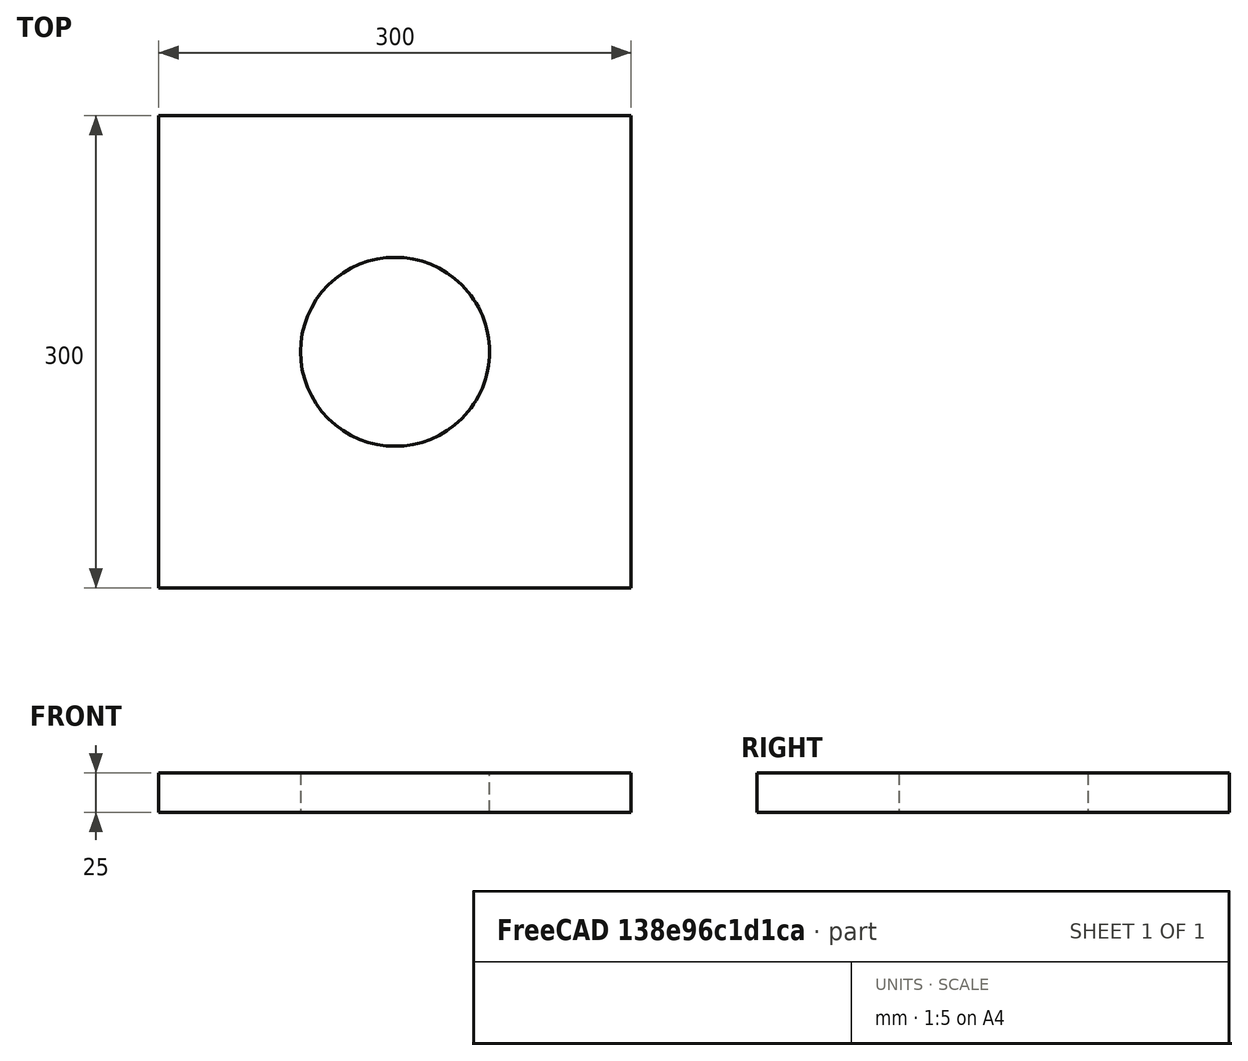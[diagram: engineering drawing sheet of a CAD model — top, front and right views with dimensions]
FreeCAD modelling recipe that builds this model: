
FCSTD DOCUMENT  (FreeCAD 0.21R33694 (Git))
Label: Lug_Pressure_Example
License: All rights reserved
LicenseURL: http://en.wikipedia.org/wiki/All_rights_reserved
objects: Part::FeaturePython×5, Sketcher::SketchObject×2, Part::Extrusion×2, Fem::FemMeshObjectPython×2, Fem::FemSolverObjectPython×1, Fem::ConstraintFixed×1, Part::MultiFuse×1, Fem::ConstraintPressure×1, App::MaterialObjectPython×1, Fem::FemResultObjectPython×1, Fem::FemAnalysis×1
note: 10 computed .brp shape members not serialized (recipe doc carries the construction recipe); baked Part::Feature solids carry a one-line shape summary decoded from their .brp

FEATURE [Sketcher::SketchObject] Sketch
  FullyConstrained = true
  Placement = pos=(150,0,0) rot=(0,0,1;0rad)
  sketch-geometry (5):
    g0: LineSegment StartX=0 StartY=0 StartZ=0 EndX=300 EndY=0 EndZ=0
    g1: LineSegment StartX=300 StartY=0 StartZ=0 EndX=300 EndY=300 EndZ=0
    g2: LineSegment StartX=300 StartY=300 StartZ=0 EndX=0 EndY=300 EndZ=0
    g3: LineSegment StartX=0 StartY=300 StartZ=0 EndX=0 EndY=0 EndZ=0
    g4: Circle CenterX=150 CenterY=150 CenterZ=0 NormalX=0 NormalY=0 NormalZ=1 AngleXU=0 Radius=60
  constraints (14):
    c: Coincident(g0,g1)
    c: Coincident(g1,g2)
    c: Coincident(g2,g3)
    c: Coincident(g3,g0)
    c: Horizontal(g0)
    c: Horizontal(g2)
    c: Vertical(g1)
    c: Vertical(g3)
    c: Coincident(g0,g-1)
    c: DistanceY(g1,g1) = 300
    c: DistanceX(g0,g0) = 300
    c: DistanceX(g0,g4) = 150
    c: DistanceY(g0,g4) = 150
    c: Radius(g4) = 60
FEATURE [Part::Extrusion] Extrude
  Base = -> Sketch
  Dir = (0,0,1)
  DirMode = 2
  FaceMakerClass = Part::FaceMakerBullseye
  LengthFwd = 25
  LengthRev = 0
  Solid = true
  Symmetric = false
FEATURE [Fem::FemSolverObjectPython] SolverCcxTools  # FEM object (typed FeaturePython)
  AnalysisType = 0
  BeamShellResultOutput3D = false
  BucklingFactors = 1
  EigenmodeHighLimit = 1000000
  EigenmodeLowLimit = 0
  EigenmodesCount = 10
  GeometricalNonlinearity = 0
  IterationsControlParameterCutb = 0.25,0.5,0.75,0.85,,,1.5,
  IterationsControlParameterIter = 4,8,9,200,10,400,,200,,
  IterationsControlParameterTimeUse = false
  IterationsThermoMechMaximum = 200
  IterationsUserDefinedIncrementations = false
  IterationsUserDefinedTimeStepLength = false
  MaterialNonlinearity = 0
  MatrixSolverType = 0
  SplitInputWriter = false
  ThermoMechSteadyState = true
  TimeEnd = 1
  TimeInitialStep = 1
FEATURE [Fem::ConstraintFixed] ConstraintFixed001
  NormalDirection = (0,-1,0)
  Normals = (16) [(0,-1,0),(0,-1,0),(0,-1,0),(0,-1,0),(0,-1,0),(0,-1,0),(0,-1,0),(0,-1,0),(0,-1,0),(0,-1,0),(0,-1,0),(0,-1,0),(0,-1,0),(0,-1,0),(0,-1,0),(0,-1,0)]
  Points = (16) [(150,0,25),(250,0,25),(350,0,25),(450,0,25),(150,0,16.6667),(250,0,16.6667),(350,0,16.6667),(450,0,16.6667),(150,0,8.33333),(250,0,8.33333),+6 more]
  References = -> [Extrude]
  Scale = 13
FEATURE [Sketcher::SketchObject] Sketch001
  FullyConstrained = true
  sketch-geometry (2):
    g0: LineSegment StartX=150 StartY=300 StartZ=0 EndX=450 EndY=0 EndZ=0
    g1: LineSegment StartX=150 StartY=0 StartZ=0 EndX=450 EndY=300 EndZ=0
  constraints (8):
    c: DistanceX(g1) = 150
    c: DistanceY(g1,g-1) = 0
    c: DistanceY(g0,g-1) = 0
    c: DistanceX(g1,g0) = 300
    c: DistanceX(g-1,g0) = 150
    c: DistanceX(g-1,g1) = 450
    c: DistanceY(g-1,g0) = 300
    c: DistanceY(g-1,g1) = 300
FEATURE [Part::Extrusion] Extrude001
  Base = -> Sketch001
  Dir = (0,0,1)
  DirMode = 0
  FaceMakerClass = Part::FaceMakerBullseye
  LengthFwd = 25
  LengthRev = 0
  Solid = false
  Symmetric = false
FEATURE [Part::FeaturePython] Slice  # WARN: FeaturePython — macro-defined, semantics opaque (R4)
  Base = -> Extrude
  Mode = 1
  Tolerance = 0
  Tools = -> [Extrude001]
FEATURE [Part::FeaturePython] Slice_child0  label="Slice.0"  # WARN: FeaturePython — macro-defined, semantics opaque (R4)
  Base = -> Slice
  FilterType = 1
  Invert = false
  OverrideMaxVal = 0
  WindowFrom = 80
  WindowTo = 100
  items = 0
FEATURE [Part::FeaturePython] Slice_child1  label="Slice.1"  # WARN: FeaturePython — macro-defined, semantics opaque (R4)
  Base = -> Slice
  FilterType = 1
  Invert = false
  OverrideMaxVal = 0
  WindowFrom = 80
  WindowTo = 100
  items = 1
FEATURE [Part::FeaturePython] Slice_child2  label="Slice.2"  # WARN: FeaturePython — macro-defined, semantics opaque (R4)
  Base = -> Slice
  FilterType = 1
  Invert = false
  OverrideMaxVal = 0
  WindowFrom = 80
  WindowTo = 100
  items = 2
FEATURE [Part::FeaturePython] Slice_child3  label="Slice.3"  # WARN: FeaturePython — macro-defined, semantics opaque (R4)
  Base = -> Slice
  FilterType = 1
  Invert = false
  OverrideMaxVal = 0
  WindowFrom = 80
  WindowTo = 100
  items = 3
FEATURE [Part::MultiFuse] Fusion001  label="Fusion_25mm"
  Shapes = -> [Slice_child0,Slice_child1,Slice_child2,Slice_child3]
FEATURE [Fem::ConstraintPressure] ConstraintPressure
  NormalDirection = (-0.92388,-0.382683,0)
  Normals = (32) [(-1,0,0),(-0.965926,-0.258819,0),(-0.866025,-0.5,0),(-0.707107,-0.707107,0),(-1,0,0),(-0.965926,-0.258819,0),(-0.866025,-0.5,0),+25 more]
  Points = (32) [(360,150,25),(357.956,165.529,25),(351.962,180,25),(342.426,192.426,25),(360,150,16.6667),(357.956,165.529,16.6667),(351.962,180,16.6667),+25 more]
  Pressure = 100
  References = -> [Fusion001]
  Scale = 5
FEATURE [App::MaterialObjectPython] MaterialSolid  # material (typed FeaturePython)
  Category = 0
  Material = AuthorAndLicense=(c) 2014 M. Münch - GNU Lesser General Public License (LGPL),CardName=Steel-St-E-315,Density=7800 kg/m^3,Father=Metal,+13 more (map truncated)
FEATURE [Fem::FemMeshObjectPython] FEMMeshGmsh  # FEM object (typed FeaturePython)
  Algorithm2D = 0
  Algorithm3D = 0
  CharacteristicLengthMax = 0
  CharacteristicLengthMin = 0
  CoherenceMesh = true
  ElementDimension = 0
  ElementOrder = 1
  GeometryTolerance = 1e-06
  GroupsOfNodes = false
  HighOrderOptimize = 0
  MeshSizeFromCurvature = 12
  OptimizeNetgen = false
  OptimizeStd = true
  Part = -> Fusion001
  RecombinationAlgorithm = 0
  Recombine3DAll = false
  RecombineAll = false
  SecondOrderLinear = false
FEATURE [Fem::FemMeshObjectPython] Result_Mesh_Volume  # FEM object (typed FeaturePython)
FEATURE [Fem::FemResultObjectPython] ResultMechanical  # FEM object (typed FeaturePython)
  CriticalStrainRatio = [0.00597029,0.00568432,0.000781889,0.00059232,0,0,0,0,0.0244211,0.238103,0.0204381,0.306029,0.0146793,0.0095596,0.00885721,-0.00147553,0.0193173,-0.000637433,0.00816778,-5.40698e-06,-0.00106923,0,0,0,0,0,-0.000124115,0.000995949,0,0,0,0,0,0,+1450 more]
  DisplacementLengths = [0,0,0,0,0.0560939,0.0565374,0.0441223,0.0440347,0.00579779,0.01282,0.00513052,0.0155958,0.0308201,0.0312226,0.0600679,0.0550825,0.0615933,0.0549481,0,0,0,0,0,0,0,0,0,0,0,0,0,0,0,0,0,0,0,0,0,0,0,0,0,0,0,0,0,0,0,0,0.056316,0.0476863,0.039436,+1431 more]
  DisplacementVectors = (1484) [(0,0,0),(0,0,0),(0,0,0),(0,0,0),(0.0541136,0.0147728,-2.94162e-05),(0.0545535,0.0148456,-2.99149e-05),(0.0440732,0.00137274,-0.00156582),+1477 more]
  Eigenmode = 0
  EigenmodeFrequency = 0
  Mesh = -> Result_Mesh_Volume
  NodeNumbers = [1,2,3,4,5,6,7,8,9,10,11,12,13,14,15,16,17,18,19,20,21,22,23,24,25,26,27,28,29,30,31,32,33,34,35,36,37,38,39,40,41,42,43,44,45,46,47,48,49,50,51,52,53,54,55,56,57,58,59,60,61,62,63,64,65,66,67,68,69,+1415 more]
  NodeStressXX = [135.516,132.384,-154.31,-170.41,4.05901,4.34584,-2.88861,-2.6569,-113.643,129.989,-153.708,72.242,156.029,138.137,-246.49,33.2696,-250.598,42.7885,237.305,-285.508,82.8152,17.2113,-17.4491,-2.92458,0.332611,-14.4779,-79.4129,144.722,+1456 more]
  NodeStressXY = [59.2172,60.0046,67.6509,64.8079,7.64991,7.68891,2.861,2.84474,115.481,101.232,118.455,100.554,115.066,125.728,-23.6303,-82.2014,-14.5146,-90.0157,102.504,107.454,24.1382,23.922,98.7662,125.202,118.542,104.558,43.2177,33.6521,12.7868,+1455 more]
  NodeStressXZ = [7.94488,-7.45438,11.6509,-14.2891,0.2585,-0.267337,0.0337621,-0.0866935,0.240917,5.31776,-9.08237,15.0603,9.9126,-12.252,3.90259,-3.31237,-10.2933,0.447224,-0.10304,0.00154787,1.84758,-1.96018,1.01006,-0.326795,0.718258,-0.0528495,-3.37012,+1457 more]
  NodeStressYY = [346.086,344.181,-356.617,-367.98,6.27523,5.4148,-1.43938,-1.27962,-154.315,-44.4993,-167.219,-105.114,115.722,161.589,-14.9553,-75.215,-85.7201,-130.45,416.154,-446.226,256.052,29.9426,-54.6516,-5.79538,9.34027,-11.9697,-203.759,335.646,+1456 more]
  NodeStressYZ = [56.1105,-53.7667,-53.9952,54.5623,0.014095,0.247001,0.159918,-0.217894,-6.64804,-10.0198,13.3054,20.0059,-2.8231,-8.31529,18.7688,0.00632823,-28.7812,-6.41711,1.1756,-2.35595,38.1679,11.5742,-0.711323,-0.433303,0.236387,-4.43818,-37.4034,+1457 more]
  NodeStressZZ = [145.912,144.221,-169.668,-177.918,-0.225086,-0.360416,0.079991,0.161102,-1.42399,30.1656,-35.6536,2.05172,-1.97303,10.2201,13.0856,-17.2894,21.3462,-7.53278,240.966,-288.067,65.3699,14.1462,-19.5207,-1.29216,3.01407,-4.08141,-72.3005,+1457 more]
  Peeq = [0.000774997,0.000737468,0.00106151,0.00107011,0,0,0,0,0.0180349,0.0921168,0.0154757,0.154184,0.00410038,0.00221304,0.00639251,-0.000376911,0.0144961,-0.000125026,0.000584541,0.000897313,-0.000228698,0,0,0,0,0,-0.000102651,-1.94047e-05,0,0,+1454 more]
  ResultType = Fem::ResultMechanical
  Stats = [0,0,0,0,0,0,0,0,0,0,0,0,0,0,0,0,0,0,0,0,0,0,0,0,0,0]
  Time = 0
FEATURE [Fem::FemAnalysis] Analysis
  Group = -> [SolverCcxTools,MaterialSolid,ConstraintFixed001,ConstraintPressure,FEMMeshGmsh,ResultMechanical]
